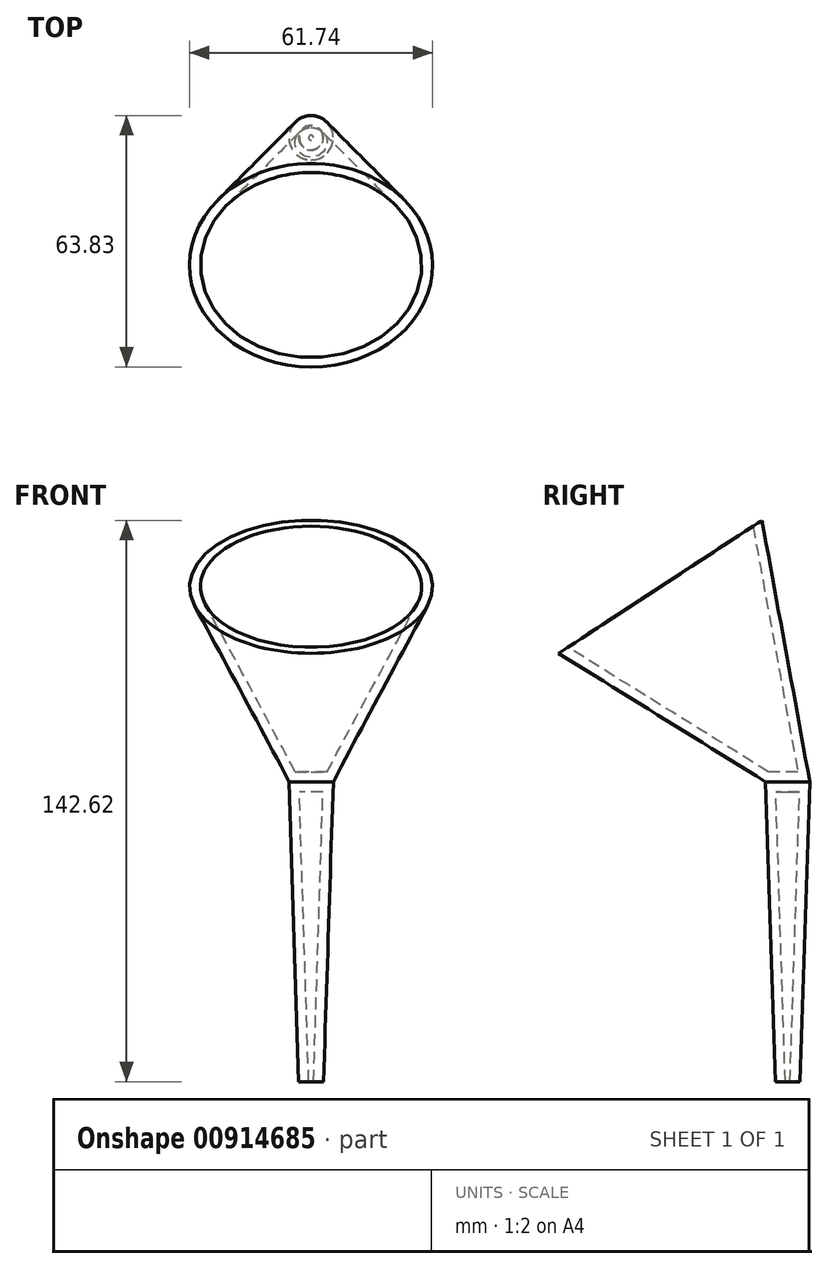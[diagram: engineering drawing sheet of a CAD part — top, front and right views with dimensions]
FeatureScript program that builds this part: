
annotation { "Feature Type Name" : "Feature", "Feature Type Description" : "" }
export const myFeature = defineFeature(function(context is Context, id is Id, definition is map)
    precondition{}
    {
        {
            var Q0;
            Q0=qCreatedBy(makeId("Top.planeOp"),FACE);
            var sketch = newSketch(context, id + "F0", { "sketchPlane" : qUnion([Q0])});
            skCircle(sketch, "E0", {"center": v(0, 0) * mm, "radius": 3.15 * mm});
            skSolve(sketch);
        }
        {
            var Q0;
            Q0=qCreatedBy(makeId("Top.planeOp"),FACE);
            cPlane(context, id + "F1", {"entities" : qUnion([Q0]), "cplaneType" : CPlaneType.OFFSET, "offset" : 76.2 * mm, "width" : 152.4 * mm, "height" : 152.4 * mm});
        }
        {
            var Q0;
            Q0=qCreatedBy(id+"F1.planeOp",FACE);
            var sketch = newSketch(context, id + "F2", { "sketchPlane" : qUnion([Q0])});
            skCircle(sketch, "E1", {"center": v(0, 0) * mm, "radius": 5.63 * mm});
            skSolve(sketch);
        }
        {
            var Q0;
            Q0=makeQuery(id+"F2.imprint","IMPRINT",FACE,{"disambiguationData":[TD([[makeQuery(id+"F2.imprint","IMPRINT",EDGE,{"derivedFrom":sQuery(id+"F2.wireOp",EDGE,"E1")}),1.0]])]});
            var Q1;
            Q1=makeQuery(id+"F0.imprint","IMPRINT",FACE,{"disambiguationData":[TD([[makeQuery(id+"F0.imprint","IMPRINT",EDGE,{"derivedFrom":sQuery(id+"F0.wireOp",EDGE,"E0")}),1.0]])]});
            loft(context, id + "F3", {"sheetProfilesArray" : [{ "sheetProfileEntities" : qUnion([Q0]) }, { "sheetProfileEntities" : qUnion([Q1]) }]});
        }
        {
            var Q0;
            Q0=qCreatedBy(makeId("Right.planeOp"),FACE);
            var sketch = newSketch(context, id + "F4", { "sketchPlane" : qUnion([Q0])});
            skLineSegment(sketch, "E2", {"start": v(0, 75.53) * mm, "end": v(-32.69, 125.52) * mm});
            skSolve(sketch);
        }
        {
            var Q0;
            Q0=sQuery(id+"F4.wireOp",EDGE,"E2");
            var Q1;
            Q1=sQuery(id+"F4.wireOp",VERTEX,"E2.end");
            cPlane(context, id + "F5", {"entities" : qUnion([Q0, Q1]), "cplaneType" : CPlaneType.CURVE_POINT, "offset" : 25.4 * mm, "width" : 152.4 * mm, "height" : 152.4 * mm});
        }
        {
            var Q0;
            Q0=qCreatedBy(id+"F5.planeOp",FACE);
            var sketch = newSketch(context, id + "F6", { "sketchPlane" : qUnion([Q0])});
            skCircle(sketch, "E3", {"center": v(0, 41.72) * mm, "radius": 30.87 * mm});
            skSolve(sketch);
        }
        {
            var Q0;
            Q0=makeQuery(id+"F6.imprint","IMPRINT",FACE,{"disambiguationData":[TD([[makeQuery(id+"F6.imprint","IMPRINT",EDGE,{"derivedFrom":sQuery(id+"F6.wireOp",EDGE,"E3")}),1.0]])]});
            var Q1;
            Q1=makeQuery(id+"F3.opLoft","CAP_FACE",FACE,{"disambiguationData":[OSD([makeQuery(id+"F2.imprint","IMPRINT",FACE,{"disambiguationData":[TD([[makeQuery(id+"F2.imprint","IMPRINT",EDGE,{"derivedFrom":sQuery(id+"F2.wireOp",EDGE,"E1")}),1.0]])]})])],"isStart":true});
            loft(context, id + "F7", {"sheetProfilesArray" : [{ "sheetProfileEntities" : qUnion([Q0]) }, { "sheetProfileEntities" : qUnion([Q1]) }]});
        }
        {
            var Q0;
            Q0=makeQuery(id+"F7.opLoft","CAP_FACE",FACE,{"disambiguationData":[OSD([makeQuery(id+"F6.imprint","IMPRINT",FACE,{"disambiguationData":[TD([[makeQuery(id+"F6.imprint","IMPRINT",EDGE,{"derivedFrom":sQuery(id+"F6.wireOp",EDGE,"E3")}),1.0]])]})])],"isStart":true});
            var Q1;
            Q1=makeQuery(id+"F3.opLoft","CAP_FACE",FACE,{"disambiguationData":[OSD([makeQuery(id+"F0.imprint","IMPRINT",FACE,{"disambiguationData":[TD([[makeQuery(id+"F0.imprint","IMPRINT",EDGE,{"derivedFrom":sQuery(id+"F0.wireOp",EDGE,"E0")}),1.0]])]})])],"isStart":true});
            shell(context, id + "F8", {"entities" : qUnion([Q0, Q1]), "thickness" : 2.54 * mm});
        }
    });
